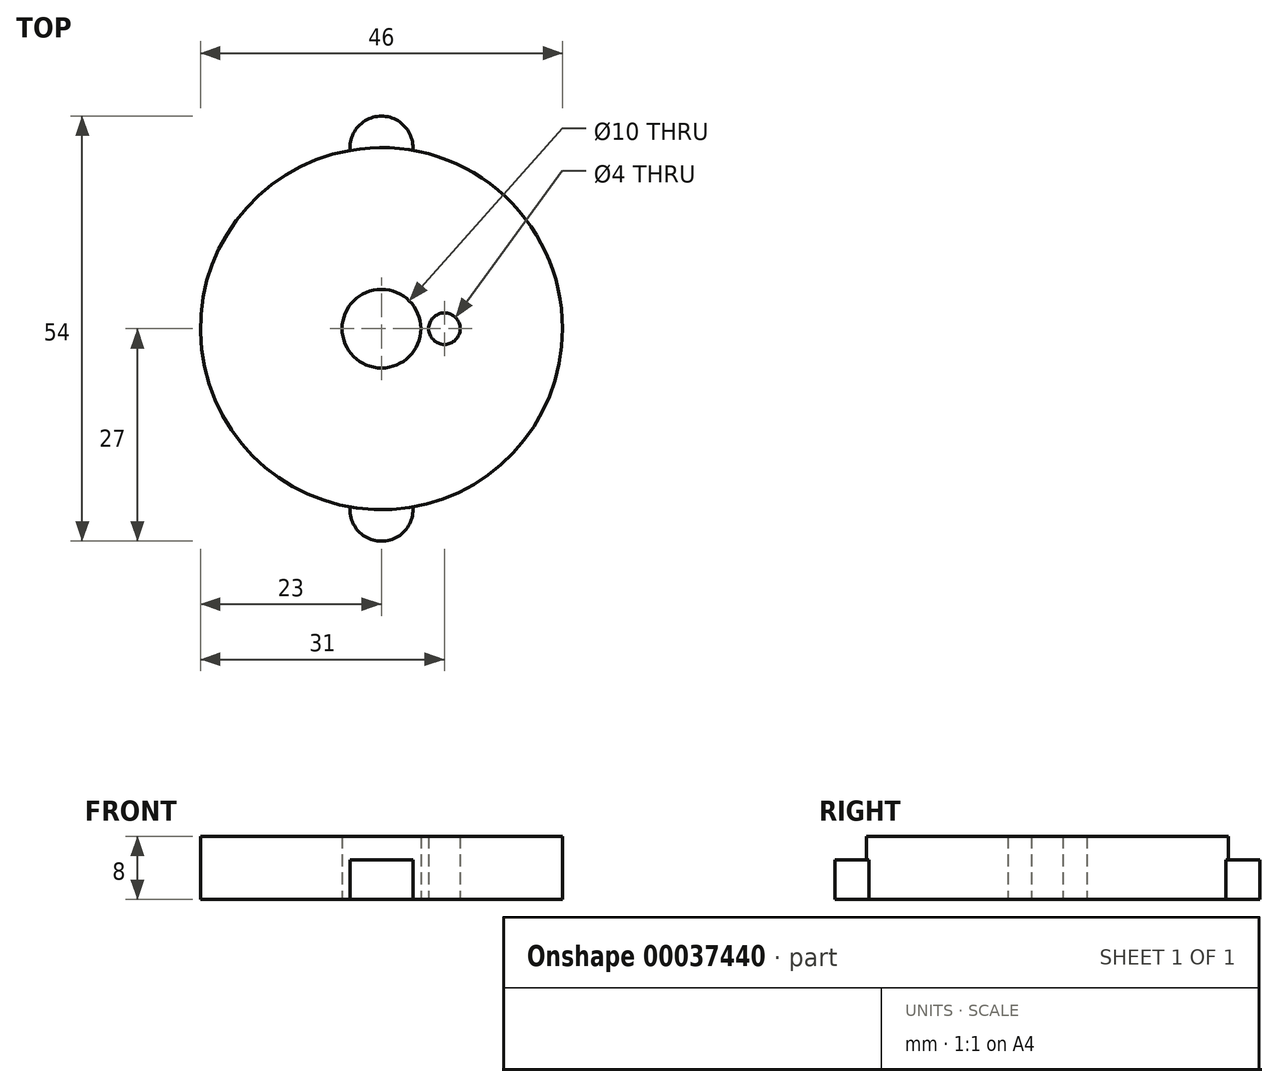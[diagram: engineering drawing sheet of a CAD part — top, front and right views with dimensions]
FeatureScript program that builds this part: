
annotation { "Feature Type Name" : "Feature", "Feature Type Description" : "" }
export const myFeature = defineFeature(function(context is Context, id is Id, definition is map)
    precondition{}
    {
        {
            var Q0;
            Q0=qCreatedBy(makeId("Top.planeOp"),FACE);
            var sketch = newSketch(context, id + "F0", { "sketchPlane" : qUnion([Q0])});
            skArc(sketch, "E0", {"start": v(-3.98, 22.65) * mm, "mid": v(-23, 0) * mm, "end": v(-3.98, -22.65) * mm});
            skArc(sketch, "E1", {"start": v(3.98, 22.65) * mm, "mid": v(0, 27) * mm, "end": v(-3.98, 22.65) * mm});
            skLineSegment(sketch, "E2", {"start": v(0, 0) * mm, "end": v(-23, 0) * mm, "construction": true});
            skArc(sketch, "E3.MirrorC", {"start": v(3.98, -22.65) * mm, "mid": v(0, -27) * mm, "end": v(-3.98, -22.65) * mm});
            skArc(sketch, "E4.trimOffspring", {"start": v(3.98, -22.65) * mm, "mid": v(23, 0) * mm, "end": v(3.98, 22.65) * mm});
            skCircle(sketch, "E5", {"center": v(0, 0) * mm, "radius": 5 * mm});
            skCircle(sketch, "E6", {"center": v(8, 0) * mm, "radius": 2 * mm});
            skSolve(sketch);
        }
        {
            var Q0;
            Q0=qSketchRegion(id+"F0",true);
            extrude(context, id + "F1", {"entities" : qUnion([Q0]), "depth" : 8 * mm});
        }
        {
            var Q0;
            Q0=makeQuery(id+"F1.opExtrude","CAP_FACE",FACE,{"disambiguationData":[OSD([sQuery(id+"F0.wireOp",EDGE,"E0"),sQuery(id+"F0.wireOp",EDGE,"E1"),sQuery(id+"F0.wireOp",EDGE,"E3.MirrorC"),sQuery(id+"F0.wireOp",EDGE,"E4.trimOffspring")])],"isStart":false});
            var sketch = newSketch(context, id + "F2", { "sketchPlane" : qUnion([Q0])});
            skArc(sketch, "E7.0", {"start": v(3.98, 22.65) * mm, "mid": v(0, 27) * mm, "end": v(-3.98, 22.65) * mm});
            skArc(sketch, "E8.0", {"start": v(3.98, -22.65) * mm, "mid": v(0, -27) * mm, "end": v(-3.98, -22.65) * mm});
            skArc(sketch, "E9", {"start": v(-3.98, -22.65) * mm, "mid": v(0, -23) * mm, "end": v(3.98, -22.65) * mm});
            skArc(sketch, "E10.trimOffspring", {"start": v(3.98, 22.65) * mm, "mid": v(0, 23) * mm, "end": v(-3.98, 22.65) * mm});
            skSolve(sketch);
        }
        {
            var Q0;
            Q0=qSketchRegion(id+"F2",true);
            extrude(context, id + "F3", {"entities" : qUnion([Q0]), "operationType" : NewBodyOperationType.REMOVE, "oppositeDirection" : true, "depth" : 3 * mm});
        }
    });
